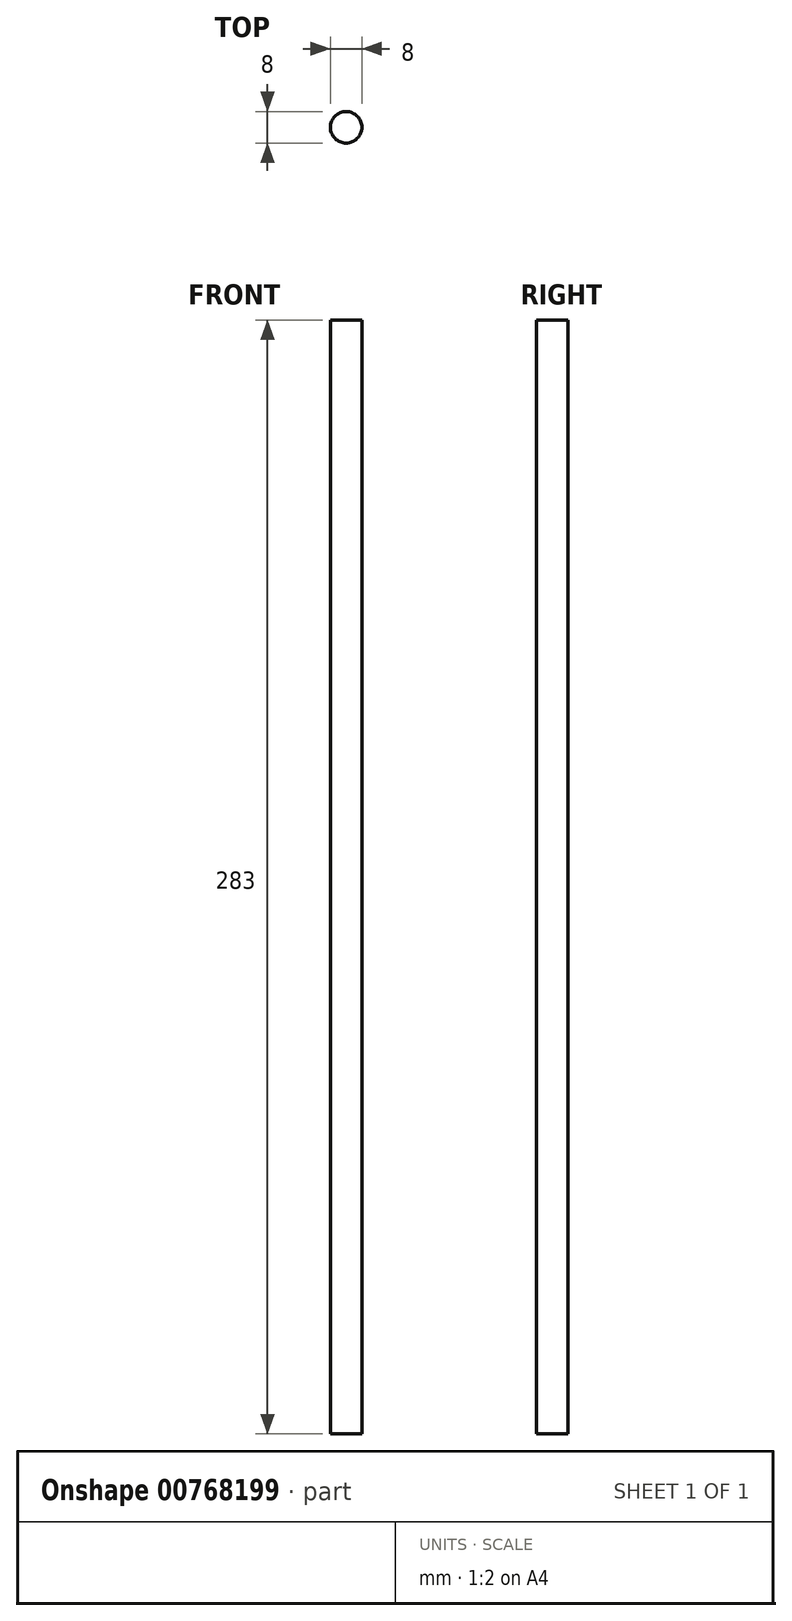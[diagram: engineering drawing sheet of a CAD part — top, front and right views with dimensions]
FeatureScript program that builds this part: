
annotation { "Feature Type Name" : "Feature", "Feature Type Description" : "" }
export const myFeature = defineFeature(function(context is Context, id is Id, definition is map)
    precondition{}
    {
        {
            var Q0;
            Q0=qCreatedBy(makeId("Top.planeOp"),FACE);
            var sketch = newSketch(context, id + "F0", { "sketchPlane" : qUnion([Q0])});
            skCircle(sketch, "E0", {"center": v(0, 0) * mm, "radius": 4 * mm});
            skSolve(sketch);
        }
        {
            var Q0;
            Q0=qSketchRegion(id+"F0",true);
            extrude(context, id + "F1", {"entities" : qUnion([Q0]), "depth" : 283 * mm, "offsetDistance" : 25 * mm});
        }
    });
